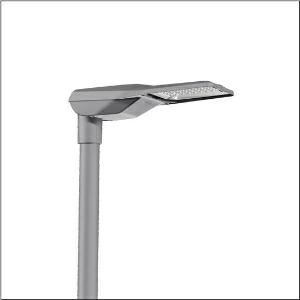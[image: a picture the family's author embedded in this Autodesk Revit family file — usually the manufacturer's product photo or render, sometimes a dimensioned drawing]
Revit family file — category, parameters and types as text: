
# Revit family: streetlight_sl_21_iq_mini___pl52_5xe2h31g08hb_1606
name_source: partatom
category: Lighting Fixtures
units: mm (PartAtom-declared; Revit-internal decimal feet)

## family parameters
Cut with Voids When Loaded = No
Host = Face
Light Source = No
Part Type = Normal
Room Calculation Point = No
Round Connector Dimension = Use Diameter
Shared = No

## types (1)
- --- (1 x LED, 9290 lm, 70.9 W, 3000K)
    Apparent Load = 71 VA
    CIE Flux Codes = 27 59 98 100 100
    Color Rendering = 70
    Color Temperature = 3000K
    Default Elevation = 1800 mm
    Description = Streetlight SL 21 iQ mini, mast luminaire, primary light control with lens, of PMMA, primary optical cover: cover, of toughened safety glass, transparent, light distribution: PL52, light emission: direct distribution, primary light characteristic: asymmetric, installation type: post-top, side-entry, LED, High Power LED, rated luminous flux: 9.290lm, luminous efficacy: 131lm/W, light colour: 730, colour temperature: 3000K, control: Street-Remote, Auto-Match, Temp-Guard, Lumen-Switch, Night-Set, Smart-Wire, Light-Fading, Desk-Remote (wireless, voltage-free reading and setting of iQ features in the workshop via application-optimized NFC function/RFID function), optimised constant luminous flux control (CLO 2.0), presetting dimming linear, mains connection: 220..240V, AC, 50/60Hz, start of lifetime: 71W, end of service life: 75W, reduction: 31W, luminaire housing, of diecast aluminium, powder-coated, Siteco® metallic grey (DB 702S), corrosivity category C5 mid according to DIN EN ISO 12944, please order mast flange separately, inclination adjustable: 0°, 5°, 10°, 15°, sealing non-destructively replaceable, multi-level sealing system, length: 628mm, width: 235mm, height: 110mm, mast flange for spigot size: 42mm (side-entry): 5XC10008XM4, 60/48mm (side-entry/post-top): 5XC10108XM2, 76/60mm (side-entry/post-top): 5XC10108XM1, protection rating (complete): IP66, insulation class (complete): insulation class II (safety insulation), certification: CE, ENEC, ENEC+, VDE, impact resistance: IK09, permissible operating ambient temperature for outdoor applications: -40..+50°C, standard-compliant lighting for roads and squares, packaging unit: 1 piece

Light Distribution: PL52
    Height = 110 mm
    Lamp = 1 x LED
    Lamp Light Flux = 9290 lm
    Lamp Power = 70.9 W
    Lamp count = 1
    Length = 625 mm
    Luminous efficacy = 131 lm/W
    Manufacturer = Siteco
    ModVariant = No
    Model = 5XE2H31G08HB
    Number of Poles = 1
    OnlyDefault = Yes
    Power Factor = 1
    Product Name = Streetlight SL 21 iQ mini | PL52
    Product group = mast luminaire | pylon top
    ProductGroupID = 6100
    Protection Class = Protection class II
    Protection Degree = IP 66
    RLX_Detail_Level = 1
    RLX_Emergency_Light_Flux = 0 lm
    RLX_Emergency_Type = 0
    RLX_Emergency_Type_DB = No
    RlxData = <blob elided: 102097 chars, md5=7addfe96>
    Socket = socket
    Standby Power = 0 W
    System Light Flux = 9290 lm
    System Power = 71 W
    Type Comments = factory setting: luminous flux: 100 % | dim-lin: 254 | 711 mA
    Type Image = l_1003519.jpg
    URL = http://relux.com
    VarID = @adj_108613
    Voltage = 0 V
    Weight = 0.00 kg
    Width = 234 mm

## geometry (parser evidence)
native form markers: Blend x4, Sweep x11
no freeform markers — native parametric forms only
